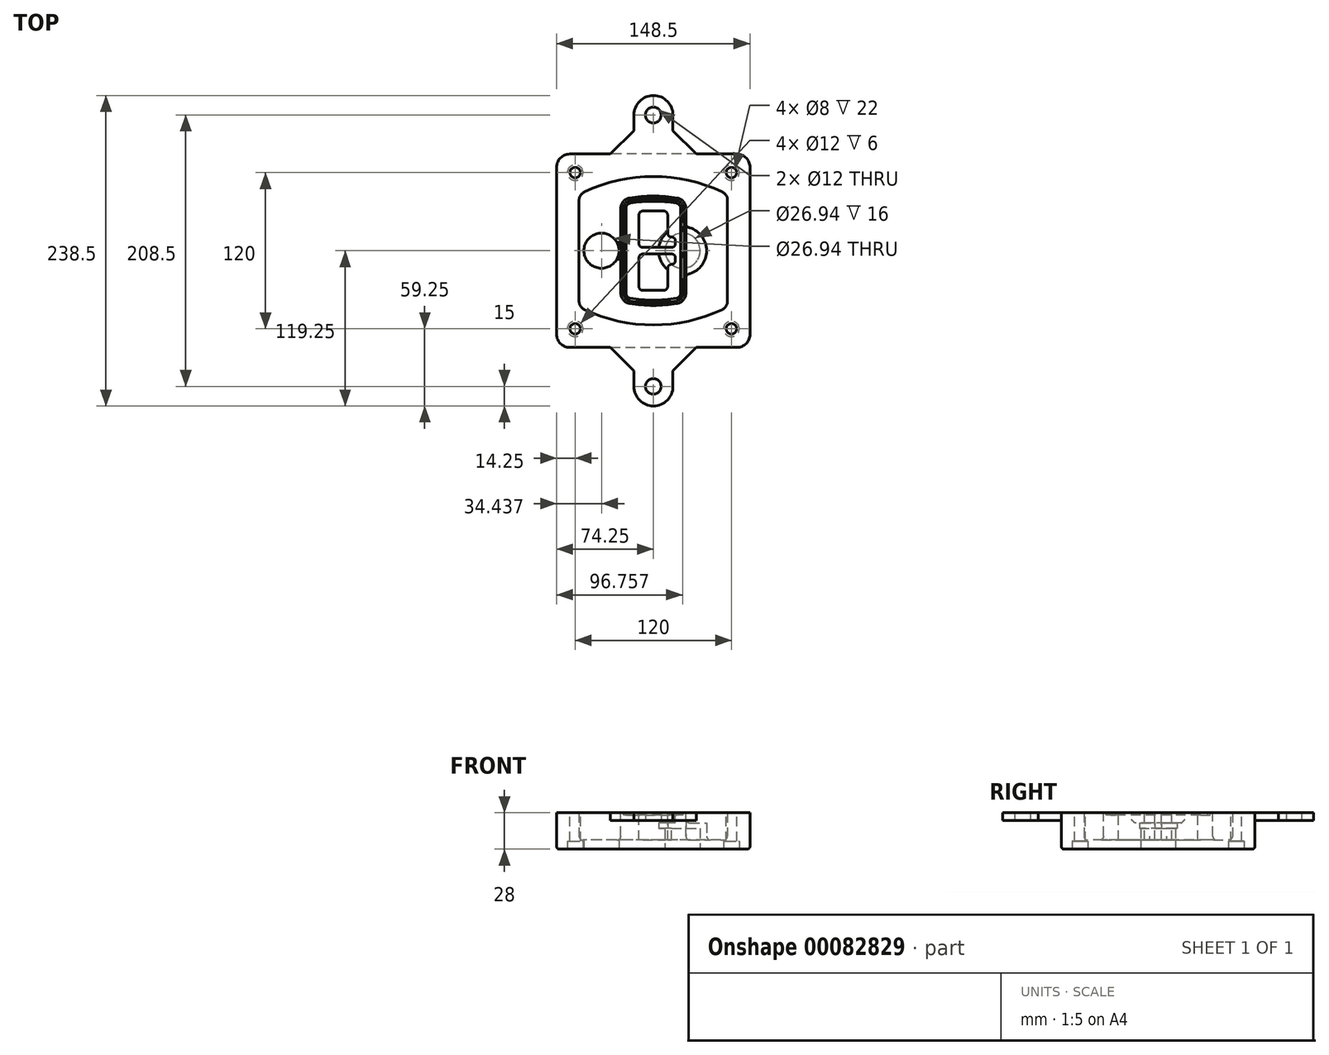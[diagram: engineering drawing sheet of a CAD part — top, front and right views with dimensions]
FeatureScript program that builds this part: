
annotation { "Feature Type Name" : "Feature", "Feature Type Description" : "" }
export const myFeature = defineFeature(function(context is Context, id is Id, definition is map)
    precondition{}
    {
        {
            var Q0;
            Q0=qCreatedBy(makeId("Top.planeOp"),FACE);
            var sketch = newSketch(context, id + "F0", { "sketchPlane" : qUnion([Q0])});
            skPoint(sketch, "E0.rect.middle", {"position": v(0, 0) * mm});
            skLineSegment(sketch, "E1.bottom", {"start": v(-64.25, -74.25) * mm, "end": v(64.25, -74.25) * mm});
            skLineSegment(sketch, "E1.top", {"start": v(-64.25, 74.25) * mm, "end": v(64.25, 74.25) * mm});
            skLineSegment(sketch, "E1.left", {"start": v(-74.25, -64.25) * mm, "end": v(-74.25, 64.25) * mm});
            skLineSegment(sketch, "E1.right", {"start": v(74.25, -64.25) * mm, "end": v(74.25, 64.25) * mm});
            skLineSegment(sketch, "E2", {"start": v(-74.25, 74.25) * mm, "end": v(74.25, -74.25) * mm, "construction": true});
            skLineSegment(sketch, "E3", {"start": v(74.25, 74.25) * mm, "end": v(-74.25, -74.25) * mm, "construction": true});
            skCircle(sketch, "E4", {"center": v(-60, 60) * mm, "radius": 4 * mm});
            skCircle(sketch, "E5", {"center": v(60, 60) * mm, "radius": 4 * mm});
            skCircle(sketch, "E6", {"center": v(60, -60) * mm, "radius": 4 * mm});
            skCircle(sketch, "E7", {"center": v(-60, -60) * mm, "radius": 4 * mm});
            skLineSegment(sketch, "E8", {"start": v(-60, 60) * mm, "end": v(60, 60) * mm, "construction": true});
            skLineSegment(sketch, "E9", {"start": v(60, 60) * mm, "end": v(60, -60) * mm, "construction": true});
            skLineSegment(sketch, "E10", {"start": v(60, -60) * mm, "end": v(-60, -60) * mm, "construction": true});
            skLineSegment(sketch, "E11", {"start": v(-60, -60) * mm, "end": v(-60, 60) * mm, "construction": true});
            skLineSegment(sketch, "E12", {"start": v(-60, 38.83) * mm, "end": v(-60, -38.83) * mm});
            skLineSegment(sketch, "E13", {"start": v(60, 38.83) * mm, "end": v(60, -38.83) * mm});
            skArc(sketch, "E14", {"start": v(54.26, 47.88) * mm, "mid": v(0, 60) * mm, "end": v(-54.26, 47.88) * mm});
            skArc(sketch, "E15", {"start": v(-54.26, -47.88) * mm, "mid": v(0, -60) * mm, "end": v(54.26, -47.88) * mm});
            skLineSegment(sketch, "E16", {"start": v(-60, 0) * mm, "end": v(60, 0) * mm, "construction": true});
            skPoint(sketch, "E17.visualSharp", {"position": v(-60, -45) * mm});
            skArc(sketch, "E17.filletArc", {"start": v(-60, -38.83) * mm, "mid": v(-58.44, -44.2) * mm, "end": v(-54.26, -47.88) * mm});
            skPoint(sketch, "E18.visualSharp", {"position": v(-60, 45) * mm});
            skArc(sketch, "E18.filletArc", {"start": v(-54.26, 47.88) * mm, "mid": v(-58.44, 44.2) * mm, "end": v(-60, 38.83) * mm});
            skPoint(sketch, "E19.visualSharp", {"position": v(60, 45) * mm});
            skArc(sketch, "E19.filletArc", {"start": v(60, 38.83) * mm, "mid": v(58.44, 44.2) * mm, "end": v(54.26, 47.88) * mm});
            skPoint(sketch, "E20.visualSharp", {"position": v(60, -45) * mm});
            skArc(sketch, "E20.filletArc", {"start": v(54.26, -47.88) * mm, "mid": v(58.44, -44.2) * mm, "end": v(60, -38.83) * mm});
            skPoint(sketch, "E21.visualSharp", {"position": v(-74.25, 74.25) * mm});
            skArc(sketch, "E21.filletArc", {"start": v(-64.25, 74.25) * mm, "mid": v(-71.32, 71.32) * mm, "end": v(-74.25, 64.25) * mm});
            skPoint(sketch, "E22.visualSharp", {"position": v(74.25, 74.25) * mm});
            skArc(sketch, "E22.filletArc", {"start": v(74.25, 64.25) * mm, "mid": v(71.32, 71.32) * mm, "end": v(64.25, 74.25) * mm});
            skPoint(sketch, "E23.visualSharp", {"position": v(74.25, -74.25) * mm});
            skArc(sketch, "E23.filletArc", {"start": v(64.25, -74.25) * mm, "mid": v(71.32, -71.32) * mm, "end": v(74.25, -64.25) * mm});
            skPoint(sketch, "E24.visualSharp", {"position": v(-74.25, -74.25) * mm});
            skArc(sketch, "E24.filletArc", {"start": v(-74.25, -64.25) * mm, "mid": v(-71.32, -71.32) * mm, "end": v(-64.25, -74.25) * mm});
            skArc(sketch, "E25.0", {"start": v(57, 38.83) * mm, "mid": v(55.9, 42.58) * mm, "end": v(52.98, 45.17) * mm});
            skLineSegment(sketch, "E25.1", {"start": v(57, 38.83) * mm, "end": v(57, -38.83) * mm});
            skArc(sketch, "E25.2", {"start": v(52.98, -45.17) * mm, "mid": v(55.9, -42.58) * mm, "end": v(57, -38.83) * mm});
            skArc(sketch, "E25.3", {"start": v(-52.98, -45.17) * mm, "mid": v(0, -57) * mm, "end": v(52.98, -45.17) * mm});
            skArc(sketch, "E25.4", {"start": v(-57, -38.83) * mm, "mid": v(-55.9, -42.58) * mm, "end": v(-52.98, -45.17) * mm});
            skArc(sketch, "E25.5", {"start": v(52.98, 45.17) * mm, "mid": v(0, 57) * mm, "end": v(-52.98, 45.17) * mm});
            skLineSegment(sketch, "E25.6", {"start": v(-57, 38.83) * mm, "end": v(-57, -38.83) * mm});
            skArc(sketch, "E25.7", {"start": v(-52.98, 45.17) * mm, "mid": v(-55.9, 42.58) * mm, "end": v(-57, 38.83) * mm});
            skArc(sketch, "E26.0", {"start": v(-55.96, 51.5) * mm, "mid": v(-61.82, 46.33) * mm, "end": v(-64, 38.83) * mm});
            skArc(sketch, "E26.1", {"start": v(55.96, 51.5) * mm, "mid": v(0, 64) * mm, "end": v(-55.96, 51.5) * mm});
            skArc(sketch, "E26.2", {"start": v(64, 38.83) * mm, "mid": v(61.82, 46.33) * mm, "end": v(55.96, 51.5) * mm});
            skLineSegment(sketch, "E26.3", {"start": v(64, 38.83) * mm, "end": v(64, -38.83) * mm});
            skArc(sketch, "E26.4", {"start": v(55.96, -51.5) * mm, "mid": v(61.82, -46.33) * mm, "end": v(64, -38.83) * mm});
            skLineSegment(sketch, "E26.5", {"start": v(-64, 38.83) * mm, "end": v(-64, -38.83) * mm});
            skArc(sketch, "E26.6", {"start": v(-55.96, -51.5) * mm, "mid": v(0, -64) * mm, "end": v(55.96, -51.5) * mm});
            skArc(sketch, "E26.7", {"start": v(-64, -38.83) * mm, "mid": v(-61.82, -46.33) * mm, "end": v(-55.96, -51.5) * mm});
            skSolve(sketch);
        }
        {
            var Q0;
            Q0=makeQuery(id+"F0.imprint","IMPRINT",FACE,{"disambiguationData":[TD([[makeQuery(id+"F0.imprint","IMPRINT",EDGE,{"derivedFrom":sQuery(id+"F0.wireOp",EDGE,"E1.bottom")}),1.0]])]});
            var Q1;
            Q1=makeQuery(id+"F0.imprint","IMPRINT",FACE,{"disambiguationData":[TD([[makeQuery(id+"F0.imprint","IMPRINT",EDGE,{"derivedFrom":sQuery(id+"F0.wireOp",EDGE,"E12")}),1.0]])]});
            var Q2;
            Q2=makeQuery(id+"F0.imprint","IMPRINT",FACE,{"disambiguationData":[TD([[makeQuery(id+"F0.imprint","IMPRINT",EDGE,{"derivedFrom":sQuery(id+"F0.wireOp",EDGE,"E25.0")}),1.0]])]});
            var Q3;
            Q3=makeQuery(id+"F0.imprint","IMPRINT",FACE,{"disambiguationData":[TD([[makeQuery(id+"F0.imprint","IMPRINT",EDGE,{"derivedFrom":sQuery(id+"F0.wireOp",EDGE,"E12")}),-1.0]])]});
            extrude(context, id + "F1", {"entities" : qUnion([Q0, Q1, Q2, Q3]), "oppositeDirection" : true, "depth" : 25 * mm});
        }
        {
            var Q0;
            Q0=makeQuery(id+"F0.imprint","IMPRINT",FACE,{"disambiguationData":[TD([[makeQuery(id+"F0.imprint","IMPRINT",EDGE,{"derivedFrom":sQuery(id+"F0.wireOp",EDGE,"E12")}),1.0]])]});
            extrude(context, id + "F2", {"entities" : qUnion([Q0]), "operationType" : NewBodyOperationType.ADD, "depth" : 3 * mm});
        }
        {
            var Q0;
            Q0=makeQuery(id+"F0.imprint","IMPRINT",FACE,{"disambiguationData":[TD([[makeQuery(id+"F0.imprint","IMPRINT",EDGE,{"derivedFrom":sQuery(id+"F0.wireOp",EDGE,"E25.0")}),1.0]])]});
            extrude(context, id + "F3", {"entities" : qUnion([Q0]), "operationType" : NewBodyOperationType.REMOVE, "oppositeDirection" : true, "depth" : 18 * mm});
        }
        {
            var Q0;
            Q0=makeQuery(id+"F2.opExtrude","CAP_FACE",FACE,{"disambiguationData":[OSD([sQuery(id+"F0.wireOp",EDGE,"E12"),sQuery(id+"F0.wireOp",EDGE,"E13"),sQuery(id+"F0.wireOp",EDGE,"E14"),sQuery(id+"F0.wireOp",EDGE,"E15"),sQuery(id+"F0.wireOp",EDGE,"E17.filletArc"),sQuery(id+"F0.wireOp",EDGE,"E18.filletArc"),sQuery(id+"F0.wireOp",EDGE,"E19.filletArc"),sQuery(id+"F0.wireOp",EDGE,"E20.filletArc"),sQuery(id+"F0.wireOp",EDGE,"E25.0"),sQuery(id+"F0.wireOp",EDGE,"E25.1"),sQuery(id+"F0.wireOp",EDGE,"E25.2"),sQuery(id+"F0.wireOp",EDGE,"E25.3"),sQuery(id+"F0.wireOp",EDGE,"E25.4"),sQuery(id+"F0.wireOp",EDGE,"E25.5"),sQuery(id+"F0.wireOp",EDGE,"E25.6"),sQuery(id+"F0.wireOp",EDGE,"E25.7")])],"isStart":false});
            var sketch = newSketch(context, id + "F4", { "sketchPlane" : qUnion([Q0])});
            skArc(sketch, "E27.0", {"start": v(-18.34, -40.45) * mm, "mid": v(0, -42) * mm, "end": v(18.34, -40.45) * mm});
            skArc(sketch, "E28.0", {"start": v(18.34, 40.45) * mm, "mid": v(0, 42) * mm, "end": v(-18.34, 40.45) * mm});
            skLineSegment(sketch, "E29", {"start": v(-25, 32.57) * mm, "end": v(-25, -32.57) * mm});
            skLineSegment(sketch, "E30", {"start": v(25, 32.57) * mm, "end": v(25, -32.57) * mm});
            skLineSegment(sketch, "E31", {"start": v(-25, 39.1) * mm, "end": v(25, 39.1) * mm, "construction": true});
            skLineSegment(sketch, "E32", {"start": v(-25, -39.1) * mm, "end": v(25, -39.1) * mm, "construction": true});
            skPoint(sketch, "E33.visualSharp", {"position": v(-25, 39.1) * mm});
            skArc(sketch, "E33.filletArc", {"start": v(-18.34, 40.45) * mm, "mid": v(-23.11, 37.73) * mm, "end": v(-25, 32.57) * mm});
            skPoint(sketch, "E34.visualSharp", {"position": v(25, 39.1) * mm});
            skArc(sketch, "E34.filletArc", {"start": v(25, 32.57) * mm, "mid": v(23.11, 37.73) * mm, "end": v(18.34, 40.45) * mm});
            skPoint(sketch, "E35.visualSharp", {"position": v(25, -39.1) * mm});
            skArc(sketch, "E35.filletArc", {"start": v(18.34, -40.45) * mm, "mid": v(23.11, -37.73) * mm, "end": v(25, -32.57) * mm});
            skPoint(sketch, "E36.visualSharp", {"position": v(-25, -39.1) * mm});
            skArc(sketch, "E36.filletArc", {"start": v(-25, -32.57) * mm, "mid": v(-23.11, -37.73) * mm, "end": v(-18.34, -40.45) * mm});
            skArc(sketch, "E37.0", {"start": v(52.98, 45.17) * mm, "mid": v(0, 57) * mm, "end": v(-52.98, 45.17) * mm});
            skArc(sketch, "E37.1", {"start": v(-52.98, 45.17) * mm, "mid": v(-55.9, 42.58) * mm, "end": v(-57, 38.83) * mm});
            skLineSegment(sketch, "E37.2", {"start": v(-57, 38.83) * mm, "end": v(-57, -38.83) * mm});
            skArc(sketch, "E37.3", {"start": v(-57, -38.83) * mm, "mid": v(-55.9, -42.58) * mm, "end": v(-52.98, -45.17) * mm});
            skArc(sketch, "E37.4", {"start": v(-52.98, -45.17) * mm, "mid": v(0, -57) * mm, "end": v(52.98, -45.17) * mm});
            skArc(sketch, "E37.5", {"start": v(52.98, -45.17) * mm, "mid": v(55.9, -42.58) * mm, "end": v(57, -38.83) * mm});
            skLineSegment(sketch, "E37.6", {"start": v(57, 38.83) * mm, "end": v(57, -38.83) * mm});
            skArc(sketch, "E37.7", {"start": v(57, 38.83) * mm, "mid": v(55.9, 42.58) * mm, "end": v(52.98, 45.17) * mm});
            skLineSegment(sketch, "E38.0", {"start": v(23, 32.57) * mm, "end": v(23, -32.57) * mm});
            skArc(sketch, "E38.1", {"start": v(18, -38.48) * mm, "mid": v(21.58, -36.44) * mm, "end": v(23, -32.57) * mm});
            skArc(sketch, "E38.2", {"start": v(-18, -38.48) * mm, "mid": v(0, -40) * mm, "end": v(18, -38.48) * mm});
            skArc(sketch, "E38.3", {"start": v(-23, -32.57) * mm, "mid": v(-21.58, -36.44) * mm, "end": v(-18, -38.48) * mm});
            skLineSegment(sketch, "E38.4", {"start": v(-23, 32.57) * mm, "end": v(-23, -32.57) * mm});
            skArc(sketch, "E38.5", {"start": v(23, 32.57) * mm, "mid": v(21.58, 36.44) * mm, "end": v(18, 38.48) * mm});
            skArc(sketch, "E38.6", {"start": v(-18, 38.48) * mm, "mid": v(-21.58, 36.44) * mm, "end": v(-23, 32.57) * mm});
            skArc(sketch, "E38.7", {"start": v(18, 38.48) * mm, "mid": v(0, 40) * mm, "end": v(-18, 38.48) * mm});
            skArc(sketch, "E39.0", {"start": v(21, 32.57) * mm, "mid": v(20.06, 35.15) * mm, "end": v(17.67, 36.5) * mm});
            skLineSegment(sketch, "E39.1", {"start": v(21, 32.57) * mm, "end": v(21, -32.57) * mm});
            skArc(sketch, "E39.2", {"start": v(17.67, -36.5) * mm, "mid": v(20.06, -35.15) * mm, "end": v(21, -32.57) * mm});
            skArc(sketch, "E39.3", {"start": v(-17.67, -36.5) * mm, "mid": v(0, -38) * mm, "end": v(17.67, -36.5) * mm});
            skArc(sketch, "E39.4", {"start": v(-21, -32.57) * mm, "mid": v(-20.06, -35.15) * mm, "end": v(-17.67, -36.5) * mm});
            skArc(sketch, "E39.5", {"start": v(17.67, 36.5) * mm, "mid": v(0, 38) * mm, "end": v(-17.67, 36.5) * mm});
            skLineSegment(sketch, "E39.6", {"start": v(-21, 32.57) * mm, "end": v(-21, -32.57) * mm});
            skArc(sketch, "E39.7", {"start": v(-17.67, 36.5) * mm, "mid": v(-20.06, 35.15) * mm, "end": v(-21, 32.57) * mm});
            skLineSegment(sketch, "E40", {"start": v(-25, 0) * mm, "end": v(25, 0) * mm, "construction": true});
            skLineSegment(sketch, "E41", {"start": v(-11, 5.5) * mm, "end": v(-11, 27.5) * mm});
            skLineSegment(sketch, "E42", {"start": v(-8, 30.5) * mm, "end": v(8, 30.5) * mm});
            skLineSegment(sketch, "E43", {"start": v(11, 27.5) * mm, "end": v(11, 13.5) * mm});
            skLineSegment(sketch, "E44", {"start": v(14, 10.5) * mm, "end": v(14, 10.5) * mm});
            skLineSegment(sketch, "E45", {"start": v(17, 7.5) * mm, "end": v(17, 5.5) * mm});
            skLineSegment(sketch, "E46", {"start": v(14, 2.5) * mm, "end": v(-8, 2.5) * mm});
            skPoint(sketch, "E47.visualSharp", {"position": v(-11, 30.5) * mm});
            skArc(sketch, "E47.filletArc", {"start": v(-8, 30.5) * mm, "mid": v(-10.12, 29.62) * mm, "end": v(-11, 27.5) * mm});
            skPoint(sketch, "E48.visualSharp", {"position": v(11, 30.5) * mm});
            skArc(sketch, "E48.filletArc", {"start": v(11, 27.5) * mm, "mid": v(10.12, 29.62) * mm, "end": v(8, 30.5) * mm});
            skPoint(sketch, "E49.visualSharp", {"position": v(11, 10.5) * mm});
            skArc(sketch, "E49.filletArc", {"start": v(11, 13.5) * mm, "mid": v(11.88, 11.38) * mm, "end": v(14, 10.5) * mm});
            skPoint(sketch, "E50.visualSharp", {"position": v(17, 10.5) * mm});
            skArc(sketch, "E50.filletArc", {"start": v(17, 7.5) * mm, "mid": v(16.12, 9.62) * mm, "end": v(14, 10.5) * mm});
            skPoint(sketch, "E51.visualSharp", {"position": v(17, 2.5) * mm});
            skArc(sketch, "E51.filletArc", {"start": v(14, 2.5) * mm, "mid": v(16.12, 3.38) * mm, "end": v(17, 5.5) * mm});
            skPoint(sketch, "E52.visualSharp", {"position": v(-11, 2.5) * mm});
            skArc(sketch, "E52.filletArc", {"start": v(-11, 5.5) * mm, "mid": v(-10.12, 3.38) * mm, "end": v(-8, 2.5) * mm});
            skLineSegment(sketch, "E53.0.MirrorCS", {"start": v(14, -2.5) * mm, "end": v(-8, -2.5) * mm});
            skArc(sketch, "E54.0.MirrorCS", {"start": v(-11, -5.5) * mm, "mid": v(-10.12, -3.38) * mm, "end": v(-8, -2.5) * mm});
            skLineSegment(sketch, "E55.0.MirrorCS", {"start": v(-11, -5.5) * mm, "end": v(-11, -27.5) * mm});
            skArc(sketch, "E56.0.MirrorCS", {"start": v(-8, -30.5) * mm, "mid": v(-10.12, -29.62) * mm, "end": v(-11, -27.5) * mm});
            skLineSegment(sketch, "E57.0.MirrorCS", {"start": v(-8, -30.5) * mm, "end": v(8, -30.5) * mm});
            skArc(sketch, "E58.0.MirrorCS", {"start": v(11, -27.5) * mm, "mid": v(10.12, -29.62) * mm, "end": v(8, -30.5) * mm});
            skLineSegment(sketch, "E59.0.MirrorCS", {"start": v(11, -27.5) * mm, "end": v(11, -13.5) * mm});
            skArc(sketch, "E60.0.MirrorCS", {"start": v(11, -13.5) * mm, "mid": v(11.88, -11.38) * mm, "end": v(14, -10.5) * mm});
            skArc(sketch, "E61.0.MirrorCS", {"start": v(17, -7.5) * mm, "mid": v(16.12, -9.62) * mm, "end": v(14, -10.5) * mm});
            skLineSegment(sketch, "E62.0.MirrorCS", {"start": v(17, -7.5) * mm, "end": v(17, -5.5) * mm});
            skArc(sketch, "E63.0.MirrorCS", {"start": v(14, -2.5) * mm, "mid": v(16.12, -3.38) * mm, "end": v(17, -5.5) * mm});
            skSolve(sketch);
        }
        {
            var Q0;
            Q0=makeQuery(id+"F4.imprint","IMPRINT",FACE,{"disambiguationData":[TD([[makeQuery(id+"F4.imprint","IMPRINT",EDGE,{"derivedFrom":sQuery(id+"F4.wireOp",EDGE,"E27.0")}),1.0]])]});
            var Q1;
            Q1=makeQuery(id+"F4.imprint","IMPRINT",FACE,{"disambiguationData":[TD([[makeQuery(id+"F4.imprint","IMPRINT",EDGE,{"derivedFrom":sQuery(id+"F4.wireOp",EDGE,"E38.0")}),-1.0]])]});
            var Q2;
            Q2=makeQuery(id+"F4.imprint","IMPRINT",FACE,{"disambiguationData":[TD([[makeQuery(id+"F4.imprint","IMPRINT",EDGE,{"derivedFrom":sQuery(id+"F4.wireOp",EDGE,"E39.0")}),1.0]])]});
            extrude(context, id + "F5", {"entities" : qUnion([Q0, Q1, Q2]), "operationType" : NewBodyOperationType.ADD, "endBound" : BoundingType.UP_TO_NEXT, "oppositeDirection" : true, "depth" : 25 * mm});
        }
        {
            var Q0;
            Q0=makeQuery(id+"F4.imprint","IMPRINT",FACE,{"disambiguationData":[TD([[makeQuery(id+"F4.imprint","IMPRINT",EDGE,{"derivedFrom":sQuery(id+"F4.wireOp",EDGE,"E38.0")}),-1.0]])]});
            extrude(context, id + "F6", {"entities" : qUnion([Q0]), "operationType" : NewBodyOperationType.REMOVE, "oppositeDirection" : true, "depth" : 2 * mm});
        }
        {
            var Q0;
            Q0=makeQuery(id+"F1.opExtrude","CAP_FACE",FACE,{"disambiguationData":[OSD([sQuery(id+"F0.wireOp",EDGE,"E1.bottom"),sQuery(id+"F0.wireOp",EDGE,"E1.top"),sQuery(id+"F0.wireOp",EDGE,"E1.left"),sQuery(id+"F0.wireOp",EDGE,"E1.right"),sQuery(id+"F0.wireOp",EDGE,"E4"),sQuery(id+"F0.wireOp",EDGE,"E5"),sQuery(id+"F0.wireOp",EDGE,"E6"),sQuery(id+"F0.wireOp",EDGE,"E7"),sQuery(id+"F0.wireOp",EDGE,"E21.filletArc"),sQuery(id+"F0.wireOp",EDGE,"E22.filletArc"),sQuery(id+"F0.wireOp",EDGE,"E23.filletArc"),sQuery(id+"F0.wireOp",EDGE,"E24.filletArc")])],"isStart":false});
            var sketch = newSketch(context, id + "F7", { "sketchPlane" : qUnion([Q0])});
            skCircle(sketch, "E64", {"center": v(22.5, 0) * mm, "radius": 13.47 * mm});
            skCircle(sketch, "E65", {"center": v(-39.81, 0) * mm, "radius": 13.47 * mm});
            skLineSegment(sketch, "E66", {"start": v(74.25, 0) * mm, "end": v(-74.25, 0) * mm});
            skCircle(sketch, "E67", {"center": v(22.5, 0) * mm, "radius": 18.47 * mm});
            skCircle(sketch, "E68", {"center": v(60, -60) * mm, "radius": 6 * mm});
            skCircle(sketch, "E69", {"center": v(-60, -60) * mm, "radius": 6 * mm});
            skCircle(sketch, "E70", {"center": v(-60, 60) * mm, "radius": 6 * mm});
            skCircle(sketch, "E71", {"center": v(60, 60) * mm, "radius": 6 * mm});
            skSolve(sketch);
        }
        {
            var Q0;
            {var subQ1=sQuery(id+"F7.wireOp",EDGE,"E66");var subQ4=sQuery(id+"F7.wireOp",EDGE,"E64");var subQ6=makeQuery(id+"F7.imprint","INTERSECT",VERTEX,{"disambiguationData":[OD(0.0)],"derivedFrom":[subQ4,subQ1]});Q0=makeQuery(id+"F7.imprint","IMPRINT",FACE,{"disambiguationData":[TD([[makeQuery(id+"F7.imprint","IMPRINT",EDGE,{"disambiguationData":[TD([[subQ6,-1.0]])],"derivedFrom":subQ4}),-1.0]])]});}
            var Q1;
            {var subQ0=sQuery(id+"F7.wireOp",EDGE,"E66");var subQ1=sQuery(id+"F7.wireOp",EDGE,"E64");var subQ3=makeQuery(id+"F7.imprint","INTERSECT",VERTEX,{"disambiguationData":[OD(0.0)],"derivedFrom":[subQ1,subQ0]});Q1=makeQuery(id+"F7.imprint","IMPRINT",FACE,{"disambiguationData":[TD([[makeQuery(id+"F7.imprint","IMPRINT",EDGE,{"disambiguationData":[TD([[subQ3,-1.0]])],"derivedFrom":subQ1}),1.0]])]});}
            var Q2;
            {var subQ0=sQuery(id+"F7.wireOp",EDGE,"E66");var subQ1=sQuery(id+"F7.wireOp",EDGE,"E64");var subQ3=makeQuery(id+"F7.imprint","INTERSECT",VERTEX,{"disambiguationData":[OD(0.0)],"derivedFrom":[subQ1,subQ0]});Q2=makeQuery(id+"F7.imprint","IMPRINT",FACE,{"disambiguationData":[TD([[makeQuery(id+"F7.imprint","IMPRINT",EDGE,{"disambiguationData":[TD([[subQ3,1.0]])],"derivedFrom":subQ1}),1.0]])]});}
            var Q3;
            {var subQ1=sQuery(id+"F7.wireOp",EDGE,"E66");var subQ4=sQuery(id+"F7.wireOp",EDGE,"E64");var subQ6=makeQuery(id+"F7.imprint","INTERSECT",VERTEX,{"disambiguationData":[OD(0.0)],"derivedFrom":[subQ4,subQ1]});Q3=makeQuery(id+"F7.imprint","IMPRINT",FACE,{"disambiguationData":[TD([[makeQuery(id+"F7.imprint","IMPRINT",EDGE,{"disambiguationData":[TD([[subQ6,1.0]])],"derivedFrom":subQ4}),-1.0]])]});}
            extrude(context, id + "F8", {"entities" : qUnion([Q0, Q1, Q2, Q3]), "operationType" : NewBodyOperationType.ADD, "oppositeDirection" : true, "depth" : 20 * mm});
        }
        {
            var Q0;
            {var subQ0=sQuery(id+"F7.wireOp",EDGE,"E66");var subQ1=sQuery(id+"F7.wireOp",EDGE,"E64");var subQ3=makeQuery(id+"F7.imprint","INTERSECT",VERTEX,{"disambiguationData":[OD(0.0)],"derivedFrom":[subQ1,subQ0]});Q0=makeQuery(id+"F7.imprint","IMPRINT",FACE,{"disambiguationData":[TD([[makeQuery(id+"F7.imprint","IMPRINT",EDGE,{"disambiguationData":[TD([[subQ3,-1.0]])],"derivedFrom":subQ1}),1.0]])]});}
            var Q1;
            {var subQ0=sQuery(id+"F7.wireOp",EDGE,"E66");var subQ1=sQuery(id+"F7.wireOp",EDGE,"E64");var subQ3=makeQuery(id+"F7.imprint","INTERSECT",VERTEX,{"disambiguationData":[OD(0.0)],"derivedFrom":[subQ1,subQ0]});Q1=makeQuery(id+"F7.imprint","IMPRINT",FACE,{"disambiguationData":[TD([[makeQuery(id+"F7.imprint","IMPRINT",EDGE,{"disambiguationData":[TD([[subQ3,1.0]])],"derivedFrom":subQ1}),1.0]])]});}
            extrude(context, id + "F9", {"entities" : qUnion([Q0, Q1]), "operationType" : NewBodyOperationType.REMOVE, "oppositeDirection" : true, "depth" : 16 * mm});
        }
        {
            var Q0;
            {var subQ0=sQuery(id+"F7.wireOp",EDGE,"E66");var subQ1=sQuery(id+"F7.wireOp",EDGE,"E65");var subQ3=makeQuery(id+"F7.imprint","INTERSECT",VERTEX,{"disambiguationData":[OD(0.0)],"derivedFrom":[subQ1,subQ0]});Q0=makeQuery(id+"F7.imprint","IMPRINT",FACE,{"disambiguationData":[TD([[makeQuery(id+"F7.imprint","IMPRINT",EDGE,{"disambiguationData":[TD([[subQ3,-1.0]])],"derivedFrom":subQ1}),1.0]])]});}
            var Q1;
            {var subQ0=sQuery(id+"F7.wireOp",EDGE,"E66");var subQ1=sQuery(id+"F7.wireOp",EDGE,"E65");var subQ3=makeQuery(id+"F7.imprint","INTERSECT",VERTEX,{"disambiguationData":[OD(0.0)],"derivedFrom":[subQ1,subQ0]});Q1=makeQuery(id+"F7.imprint","IMPRINT",FACE,{"disambiguationData":[TD([[makeQuery(id+"F7.imprint","IMPRINT",EDGE,{"disambiguationData":[TD([[subQ3,1.0]])],"derivedFrom":subQ1}),1.0]])]});}
            extrude(context, id + "F10", {"entities" : qUnion([Q0, Q1]), "operationType" : NewBodyOperationType.REMOVE, "oppositeDirection" : true, "depth" : 25 * mm});
        }
        {
            var Q0;
            Q0=makeQuery(id+"F7.imprint","IMPRINT",FACE,{"disambiguationData":[TD([[makeQuery(id+"F7.imprint","IMPRINT",EDGE,{"derivedFrom":sQuery(id+"F7.wireOp",EDGE,"E68")}),1.0]])]});
            var Q1;
            Q1=makeQuery(id+"F7.imprint","IMPRINT",FACE,{"disambiguationData":[TD([[makeQuery(id+"F7.imprint","IMPRINT",EDGE,{"derivedFrom":makeQuery(id+"F1.opExtrude","CAP_EDGE",EDGE,{"disambiguationData":[OSD([sQuery(id+"F0.wireOp",EDGE,"E5")])],"isStart":false})}),-1.0]])]});
            var Q2;
            Q2=makeQuery(id+"F7.imprint","IMPRINT",FACE,{"disambiguationData":[TD([[makeQuery(id+"F7.imprint","IMPRINT",EDGE,{"derivedFrom":sQuery(id+"F7.wireOp",EDGE,"E69")}),1.0]])]});
            var Q3;
            Q3=makeQuery(id+"F7.imprint","IMPRINT",FACE,{"disambiguationData":[TD([[makeQuery(id+"F7.imprint","IMPRINT",EDGE,{"derivedFrom":makeQuery(id+"F1.opExtrude","CAP_EDGE",EDGE,{"disambiguationData":[OSD([sQuery(id+"F0.wireOp",EDGE,"E4")])],"isStart":false})}),-1.0]])]});
            var Q4;
            Q4=makeQuery(id+"F7.imprint","IMPRINT",FACE,{"disambiguationData":[TD([[makeQuery(id+"F7.imprint","IMPRINT",EDGE,{"derivedFrom":sQuery(id+"F7.wireOp",EDGE,"E70")}),1.0]])]});
            var Q5;
            Q5=makeQuery(id+"F7.imprint","IMPRINT",FACE,{"disambiguationData":[TD([[makeQuery(id+"F7.imprint","IMPRINT",EDGE,{"derivedFrom":makeQuery(id+"F1.opExtrude","CAP_EDGE",EDGE,{"disambiguationData":[OSD([sQuery(id+"F0.wireOp",EDGE,"E7")])],"isStart":false})}),-1.0]])]});
            var Q6;
            Q6=makeQuery(id+"F7.imprint","IMPRINT",FACE,{"disambiguationData":[TD([[makeQuery(id+"F7.imprint","IMPRINT",EDGE,{"derivedFrom":sQuery(id+"F7.wireOp",EDGE,"E71")}),1.0]])]});
            var Q7;
            Q7=makeQuery(id+"F7.imprint","IMPRINT",FACE,{"disambiguationData":[TD([[makeQuery(id+"F7.imprint","IMPRINT",EDGE,{"derivedFrom":makeQuery(id+"F1.opExtrude","CAP_EDGE",EDGE,{"disambiguationData":[OSD([sQuery(id+"F0.wireOp",EDGE,"E6")])],"isStart":false})}),-1.0]])]});
            extrude(context, id + "F11", {"entities" : qUnion([Q0, Q1, Q2, Q3, Q4, Q5, Q6, Q7]), "operationType" : NewBodyOperationType.REMOVE, "oppositeDirection" : true, "depth" : 6 * mm});
        }
        {
            var Q0;
            Q0=makeQuery(id+"F9.boolean.opBoolean","COPY",FACE,{"derivedFrom":makeQuery(id+"F9.opExtrude","CAP_FACE",FACE,{"disambiguationData":[OSD([sQuery(id+"F7.wireOp",EDGE,"E64")])],"isStart":false})});
            var sketch = newSketch(context, id + "F12", { "sketchPlane" : qUnion([Q0])});
            skArc(sketch, "E72.0", {"start": v(11, 14.45) * mm, "mid": v(6.45, 9.13) * mm, "end": v(4.2, 2.5) * mm});
            skArc(sketch, "E72.1", {"start": v(4.2, -2.5) * mm, "mid": v(6.45, -9.13) * mm, "end": v(11, -14.45) * mm});
            skLineSegment(sketch, "E73", {"start": v(4.2, -2.5) * mm, "end": v(14, -2.5) * mm});
            skLineSegment(sketch, "E74.0", {"start": v(14, 2.5) * mm, "end": v(4.2, 2.5) * mm});
            skArc(sketch, "E74.1", {"start": v(14, 2.5) * mm, "mid": v(16.12, 3.38) * mm, "end": v(17, 5.5) * mm});
            skLineSegment(sketch, "E74.2", {"start": v(17, 7.5) * mm, "end": v(17, 5.5) * mm});
            skArc(sketch, "E74.3", {"start": v(17, 7.5) * mm, "mid": v(16.12, 9.62) * mm, "end": v(14, 10.5) * mm});
            skArc(sketch, "E74.4", {"start": v(11, 13.5) * mm, "mid": v(11.88, 11.38) * mm, "end": v(14, 10.5) * mm});
            skLineSegment(sketch, "E74.5", {"start": v(11, 14.45) * mm, "end": v(11, 13.5) * mm});
            skLineSegment(sketch, "E74.7", {"start": v(14, -2.5) * mm, "end": v(4.2, -2.5) * mm});
            skArc(sketch, "E74.8", {"start": v(14, -2.5) * mm, "mid": v(16.12, -3.38) * mm, "end": v(17, -5.5) * mm});
            skLineSegment(sketch, "E74.9", {"start": v(17, -7.5) * mm, "end": v(17, -5.5) * mm});
            skArc(sketch, "E74.10", {"start": v(17, -7.5) * mm, "mid": v(16.12, -9.62) * mm, "end": v(14, -10.5) * mm});
            skArc(sketch, "E74.11", {"start": v(11, -13.5) * mm, "mid": v(11.88, -11.38) * mm, "end": v(14, -10.5) * mm});
            skLineSegment(sketch, "E74.12", {"start": v(11, -14.45) * mm, "end": v(11, -13.5) * mm});
            skPoint(sketch, "E75.orphan", {"position": v(11, -27.5) * mm});
            skPoint(sketch, "E76.orphan", {"position": v(-8, -2.5) * mm});
            skPoint(sketch, "E77.orphan", {"position": v(-8, 2.5) * mm});
            skPoint(sketch, "E78.orphan", {"position": v(11, 27.5) * mm});
            skSolve(sketch);
        }
        {
            var Q0;
            {var subQ7=sQuery(id+"F12.wireOp",EDGE,"E72.0");var subQ14=sQuery(id+"F12.wireOp",EDGE,"E72.1");var subQ16=sQuery(id+"F12.wireOp",EDGE,"E74.1");var subQ18=sQuery(id+"F12.wireOp",EDGE,"E74.8");Q0=qUnion([makeQuery(id+"F12.imprint","IMPRINT",FACE,{"disambiguationData":[TD([[makeQuery(id+"F12.imprint","IMPRINT",EDGE,{"derivedFrom":subQ7}),1.0]])]}),makeQuery(id+"F12.imprint","IMPRINT",FACE,{"disambiguationData":[TD([[makeQuery(id+"F12.imprint","IMPRINT",EDGE,{"derivedFrom":subQ14}),1.0]])]}),makeQuery(id+"F12.imprint","IMPRINT",FACE,{"disambiguationData":[TD([[makeQuery(id+"F12.imprint","IMPRINT",EDGE,{"derivedFrom":subQ16}),1.0]])]}),makeQuery(id+"F12.imprint","IMPRINT",FACE,{"disambiguationData":[TD([[makeQuery(id+"F12.imprint","IMPRINT",EDGE,{"derivedFrom":subQ18}),-1.0]])]})]);}
            var Q1;
            Q1=makeQuery(id+"F5.boolean.opBoolean","SPLIT",FACE,{"disambiguationData":[TD([makeQuery(id+"F5.opExtrude","SWEPT_FACE",FACE,{"disambiguationData":[OSD([sQuery(id+"F4.wireOp",EDGE,"E41")])]})])],"derivedFrom":makeQuery(id+"F3.boolean.opBoolean","COPY",FACE,{"derivedFrom":makeQuery(id+"F3.opExtrude","CAP_FACE",FACE,{"disambiguationData":[OSD([sQuery(id+"F0.wireOp",EDGE,"E25.0"),sQuery(id+"F0.wireOp",EDGE,"E25.1"),sQuery(id+"F0.wireOp",EDGE,"E25.2"),sQuery(id+"F0.wireOp",EDGE,"E25.3"),sQuery(id+"F0.wireOp",EDGE,"E25.4"),sQuery(id+"F0.wireOp",EDGE,"E25.5"),sQuery(id+"F0.wireOp",EDGE,"E25.6"),sQuery(id+"F0.wireOp",EDGE,"E25.7")])],"isStart":false})})});
            extrude(context, id + "F13", {"entities" : qUnion([Q0]), "operationType" : NewBodyOperationType.REMOVE, "endBound" : BoundingType.UP_TO_SURFACE, "endBoundEntityFace" : qUnion([Q1]), "depth" : 25 * mm});
        }
        {
            var Q0;
            Q0=makeQuery(id+"F3.boolean.opBoolean","COPY",EDGE,{"derivedFrom":makeQuery(id+"F3.opExtrude","CAP_EDGE",EDGE,{"disambiguationData":[OSD([sQuery(id+"F0.wireOp",EDGE,"E25.6")])],"isStart":false})});
            var Q1;
            Q1=makeQuery(id+"F8.boolean.opBoolean","INTERSECT",EDGE,{"derivedFrom":[makeQuery(id+"F5.opExtrude","SWEPT_FACE",FACE,{"disambiguationData":[OSD([sQuery(id+"F4.wireOp",EDGE,"E30")])]}),makeQuery(id+"F8.opExtrude","CAP_FACE",FACE,{"disambiguationData":[OSD([sQuery(id+"F7.wireOp",EDGE,"E67")])],"isStart":false})]});
            var Q2;
            Q2=makeQuery(id+"F8.boolean.opBoolean","INTERSECT",EDGE,{"disambiguationData":[OD(1.0)],"derivedFrom":[makeQuery(id+"F5.opExtrude","SWEPT_FACE",FACE,{"disambiguationData":[OSD([sQuery(id+"F4.wireOp",EDGE,"E30")])]}),makeQuery(id+"F8.opExtrude","SWEPT_FACE",FACE,{"disambiguationData":[OSD([sQuery(id+"F7.wireOp",EDGE,"E67")])]})]});
            var Q3;
            {var subQ0=sQuery(id+"F4.wireOp",EDGE,"E30");Q3=makeQuery(id+"F8.boolean.opBoolean","SPLIT",EDGE,{"disambiguationData":[TD([makeQuery(id+"F5.opExtrude","SWEPT_FACE",FACE,{"disambiguationData":[OSD([sQuery(id+"F4.wireOp",EDGE,"E35.filletArc")])]})])],"derivedFrom":makeQuery(id+"F5.opExtrude","CAP_EDGE",EDGE,{"disambiguationData":[OSD([subQ0])],"isStart":false})});}
            var Q4;
            {var subQ0=sQuery(id+"F0.wireOp",EDGE,"E25.7");var subQ1=sQuery(id+"F0.wireOp",EDGE,"E25.1");var subQ2=sQuery(id+"F0.wireOp",EDGE,"E25.6");var subQ3=sQuery(id+"F0.wireOp",EDGE,"E25.5");var subQ4=sQuery(id+"F0.wireOp",EDGE,"E25.4");var subQ5=sQuery(id+"F0.wireOp",EDGE,"E25.0");var subQ6=sQuery(id+"F0.wireOp",EDGE,"E25.2");var subQ7=sQuery(id+"F0.wireOp",EDGE,"E25.3");Q4=makeQuery(id+"F8.boolean.opBoolean","INTERSECT",EDGE,{"derivedFrom":[makeQuery(id+"F5.boolean.opBoolean","SPLIT",FACE,{"disambiguationData":[TD([makeQuery(id+"F2.opExtrude","SWEPT_FACE",FACE,{"disambiguationData":[OSD([subQ5])]})])],"derivedFrom":makeQuery(id+"F3.boolean.opBoolean","COPY",FACE,{"derivedFrom":makeQuery(id+"F3.opExtrude","CAP_FACE",FACE,{"disambiguationData":[OSD([subQ5,subQ1,subQ6,subQ7,subQ4,subQ3,subQ2,subQ0])],"isStart":false})})}),makeQuery(id+"F8.opExtrude","SWEPT_FACE",FACE,{"disambiguationData":[OSD([sQuery(id+"F7.wireOp",EDGE,"E67")])]})]});}
            var Q5;
            Q5=makeQuery(id+"F8.boolean.opBoolean","INTERSECT",EDGE,{"disambiguationData":[OD(0.0)],"derivedFrom":[makeQuery(id+"F5.opExtrude","SWEPT_FACE",FACE,{"disambiguationData":[OSD([sQuery(id+"F4.wireOp",EDGE,"E30")])]}),makeQuery(id+"F8.opExtrude","SWEPT_FACE",FACE,{"disambiguationData":[OSD([sQuery(id+"F7.wireOp",EDGE,"E67")])]})]});
            fillet(context, id + "F14", {"entities" : qUnion([Q0, Q1, Q2, Q3, Q4, Q5]), "radius" : 3 * mm, "tangentPropagation" : true, "allowEdgeOverflow" : false});
        }
        {
            var Q0;
            Q0=makeQuery(id+"F1.opExtrude","CAP_EDGE",EDGE,{"disambiguationData":[OSD([sQuery(id+"F0.wireOp",EDGE,"E1.bottom")])],"isStart":false});
            fillet(context, id + "F15", {"entities" : qUnion([Q0]), "radius" : 2 * mm, "tangentPropagation" : true, "allowEdgeOverflow" : false});
        }
        {
            var Q0;
            {var subQ0=sQuery(id+"F0.wireOp",EDGE,"E22.filletArc");var subQ1=sQuery(id+"F0.wireOp",EDGE,"E7");var subQ2=sQuery(id+"F0.wireOp",EDGE,"E6");var subQ3=sQuery(id+"F0.wireOp",EDGE,"E5");var subQ4=sQuery(id+"F0.wireOp",EDGE,"E4");var subQ5=sQuery(id+"F0.wireOp",EDGE,"E1.bottom");var subQ6=sQuery(id+"F0.wireOp",EDGE,"E21.filletArc");var subQ7=sQuery(id+"F0.wireOp",EDGE,"E1.top");var subQ8=sQuery(id+"F0.wireOp",EDGE,"E1.left");var subQ9=sQuery(id+"F0.wireOp",EDGE,"E1.right");var subQ10=sQuery(id+"F0.wireOp",EDGE,"E23.filletArc");var subQ11=sQuery(id+"F0.wireOp",EDGE,"E24.filletArc");Q0=makeQuery(id+"F2.boolean.opBoolean","SPLIT",FACE,{"disambiguationData":[TD([makeQuery(id+"F1.opExtrude","SWEPT_FACE",FACE,{"disambiguationData":[OSD([subQ5])]})])],"derivedFrom":makeQuery(id+"F1.opExtrude","CAP_FACE",FACE,{"disambiguationData":[OSD([subQ5,subQ7,subQ8,subQ9,subQ4,subQ3,subQ2,subQ1,subQ6,subQ0,subQ10,subQ11])],"isStart":true})});}
            var sketch = newSketch(context, id + "F16", { "sketchPlane" : qUnion([Q0])});
            skLineSegment(sketch, "E79.0", {"start": v(-64.25, 74.25) * mm, "end": v(64.25, 74.25) * mm});
            skArc(sketch, "E79.1", {"start": v(-64.25, 74.25) * mm, "mid": v(-71.32, 71.32) * mm, "end": v(-74.25, 64.25) * mm});
            skLineSegment(sketch, "E79.2", {"start": v(-74.25, -64.25) * mm, "end": v(-74.25, 64.25) * mm});
            skArc(sketch, "E79.3", {"start": v(-74.25, -64.25) * mm, "mid": v(-71.32, -71.32) * mm, "end": v(-64.25, -74.25) * mm});
            skCircle(sketch, "E79.4", {"center": v(-60, -60) * mm, "radius": 4 * mm});
            skCircle(sketch, "E79.5", {"center": v(-60, 60) * mm, "radius": 4 * mm});
            skCircle(sketch, "E79.6", {"center": v(60, 60) * mm, "radius": 4 * mm});
            skArc(sketch, "E79.7", {"start": v(74.25, 64.25) * mm, "mid": v(71.32, 71.32) * mm, "end": v(64.25, 74.25) * mm});
            skLineSegment(sketch, "E79.8", {"start": v(74.25, -64.25) * mm, "end": v(74.25, 64.25) * mm});
            skArc(sketch, "E79.9", {"start": v(64.25, -74.25) * mm, "mid": v(71.32, -71.32) * mm, "end": v(74.25, -64.25) * mm});
            skLineSegment(sketch, "E79.10", {"start": v(-64.25, -74.25) * mm, "end": v(64.25, -74.25) * mm});
            skCircle(sketch, "E79.11", {"center": v(60, -60) * mm, "radius": 4 * mm});
            skArc(sketch, "E79.12", {"start": v(-54.26, -47.88) * mm, "mid": v(0, -60) * mm, "end": v(54.26, -47.88) * mm});
            skArc(sketch, "E79.13", {"start": v(54.26, -47.88) * mm, "mid": v(58.44, -44.2) * mm, "end": v(60, -38.83) * mm});
            skLineSegment(sketch, "E79.14", {"start": v(60, 38.83) * mm, "end": v(60, -38.83) * mm});
            skArc(sketch, "E79.15", {"start": v(60, 38.83) * mm, "mid": v(58.44, 44.2) * mm, "end": v(54.26, 47.88) * mm});
            skArc(sketch, "E79.16", {"start": v(54.26, 47.88) * mm, "mid": v(0, 60) * mm, "end": v(-54.26, 47.88) * mm});
            skArc(sketch, "E79.17", {"start": v(-54.26, 47.88) * mm, "mid": v(-58.44, 44.2) * mm, "end": v(-60, 38.83) * mm});
            skLineSegment(sketch, "E79.18", {"start": v(-60, 38.83) * mm, "end": v(-60, -38.83) * mm});
            skArc(sketch, "E79.19", {"start": v(-60, -38.83) * mm, "mid": v(-58.44, -44.2) * mm, "end": v(-54.26, -47.88) * mm});
            skLineSegment(sketch, "E80", {"start": v(0, 74.25) * mm, "end": v(0, 104.25) * mm, "construction": true});
            skPoint(sketch, "E80.endSnap0", {"position": v(0, 74.25) * mm});
            skCircle(sketch, "E81", {"center": v(0, 104.25) * mm, "radius": 6 * mm});
            skLineSegment(sketch, "E82", {"start": v(-32.9, 74.25) * mm, "end": v(-14.9, 92.25) * mm});
            skLineSegment(sketch, "E83", {"start": v(-14.9, 92.25) * mm, "end": v(-14.9, 104.25) * mm});
            skLineSegment(sketch, "E84", {"start": v(33.1, 74.25) * mm, "end": v(15.1, 92.25) * mm});
            skLineSegment(sketch, "E85", {"start": v(15.1, 92.25) * mm, "end": v(15.1, 104.25) * mm});
            skArc(sketch, "E86", {"start": v(15.1, 104.25) * mm, "mid": v(0.1, 119.25) * mm, "end": v(-14.9, 104.25) * mm});
            skLineSegment(sketch, "E87", {"start": v(-74.25, 0) * mm, "end": v(74.25, 0) * mm, "construction": true});
            skLineSegment(sketch, "E88.MirrorCS", {"start": v(15.1, 92.25) * mm, "end": v(3.1, 92.25) * mm});
            skLineSegment(sketch, "E89.MirrorCS", {"start": v(33.1, -74.25) * mm, "end": v(15.1, -92.25) * mm});
            skLineSegment(sketch, "E90.MirrorCS", {"start": v(15.1, -92.25) * mm, "end": v(15.1, -104.25) * mm});
            skArc(sketch, "E91.MirrorCS", {"start": v(15.1, -104.25) * mm, "mid": v(0.1, -119.25) * mm, "end": v(-14.9, -104.25) * mm});
            skLineSegment(sketch, "E92.MirrorCS", {"start": v(-14.9, -92.25) * mm, "end": v(-14.9, -104.25) * mm});
            skLineSegment(sketch, "E93.MirrorCS", {"start": v(-32.9, -74.25) * mm, "end": v(-14.9, -92.25) * mm});
            skCircle(sketch, "E94.MirrorC", {"center": v(0, -104.25) * mm, "radius": 6 * mm});
            skSolve(sketch);
        }
        {
            var Q0;
            Q0 = qSketchRegion(id + "F16", true);
            extrude(context, id + "F17", {"entities" : qUnion([Q0]), "operationType" : NewBodyOperationType.ADD, "endBound" : BoundingType.SYMMETRIC, "depth" : 6 * mm});
        }
    });
